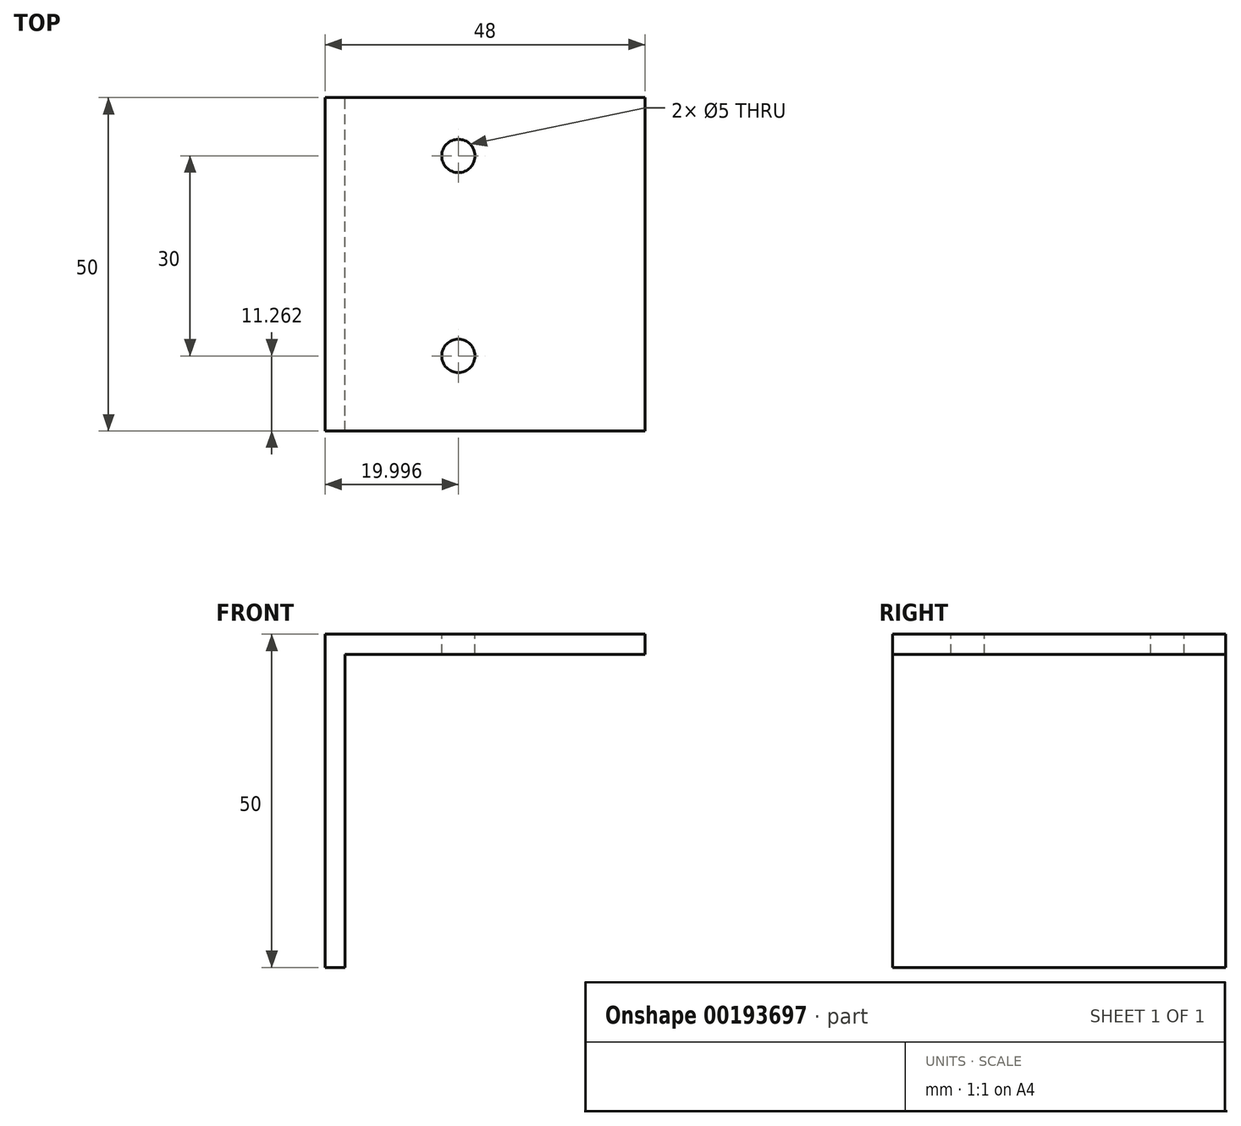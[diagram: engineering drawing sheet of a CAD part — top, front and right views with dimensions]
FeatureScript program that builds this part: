
annotation { "Feature Type Name" : "Feature", "Feature Type Description" : "" }
export const myFeature = defineFeature(function(context is Context, id is Id, definition is map)
    precondition{}
    {
        {
            var Q0;
            Q0=qCreatedBy(makeId("Front.planeOp"),FACE);
            var sketch = newSketch(context, id + "F0", { "sketchPlane" : qUnion([Q0])});
            skLineSegment(sketch, "E0", {"start": v(-55.55, 33.9) * mm, "end": v(-55.55, -16.1) * mm});
            skLineSegment(sketch, "E1", {"start": v(-55.55, -16.1) * mm, "end": v(-52.55, -16.1) * mm});
            skLineSegment(sketch, "E2", {"start": v(-52.55, -16.1) * mm, "end": v(-52.55, 30.9) * mm});
            skLineSegment(sketch, "E3", {"start": v(-52.55, 30.9) * mm, "end": v(-7.55, 30.9) * mm});
            skLineSegment(sketch, "E4", {"start": v(-7.55, 30.9) * mm, "end": v(-7.55, 33.9) * mm});
            skLineSegment(sketch, "E5", {"start": v(-7.55, 33.9) * mm, "end": v(-55.55, 33.9) * mm});
            skSolve(sketch);
        }
        {
            var Q0;
            Q0=makeQuery(id+"F0.imprint","IMPRINT",FACE,{"disambiguationData":[TD([[makeQuery(id+"F0.imprint","IMPRINT",EDGE,{"derivedFrom":sQuery(id+"F0.wireOp",EDGE,"E0")}),1.0]])]});
            extrude(context, id + "F1", {"entities" : qUnion([Q0]), "depth" : 50 * mm});
        }
        {
            var Q0;
            Q0=makeQuery(id+"F1.opExtrude","SWEPT_FACE",FACE,{"disambiguationData":[OSD([sQuery(id+"F0.wireOp",EDGE,"E5")])]});
            var sketch = newSketch(context, id + "F2", { "sketchPlane" : qUnion([Q0])});
            skCircle(sketch, "E6", {"center": v(-35.55, -8.74) * mm, "radius": 2.5 * mm});
            skCircle(sketch, "E7", {"center": v(-35.55, -38.74) * mm, "radius": 2.5 * mm});
            skSolve(sketch);
        }
        {
            var Q0;
            Q0=makeQuery(id+"F2.imprint","IMPRINT",FACE,{"disambiguationData":[TD([[makeQuery(id+"F2.imprint","IMPRINT",EDGE,{"derivedFrom":sQuery(id+"F2.wireOp",EDGE,"E6")}),1.0]])]});
            var Q1;
            Q1=makeQuery(id+"F2.imprint","IMPRINT",FACE,{"disambiguationData":[TD([[makeQuery(id+"F2.imprint","IMPRINT",EDGE,{"derivedFrom":sQuery(id+"F2.wireOp",EDGE,"E7")}),1.0]])]});
            var Q2;
            Q2=sQuery(id+"F2.wireOp",EDGE,"E7");
            var Q3;
            Q3=sQuery(id+"F2.wireOp",EDGE,"E6");
            extrude(context, id + "F3", {"entities" : qUnion([Q0, Q1]), "operationType" : NewBodyOperationType.REMOVE, "surfaceEntities" : qUnion([Q2, Q3]), "oppositeDirection" : true, "depth" : 25 * mm});
        }
    });
